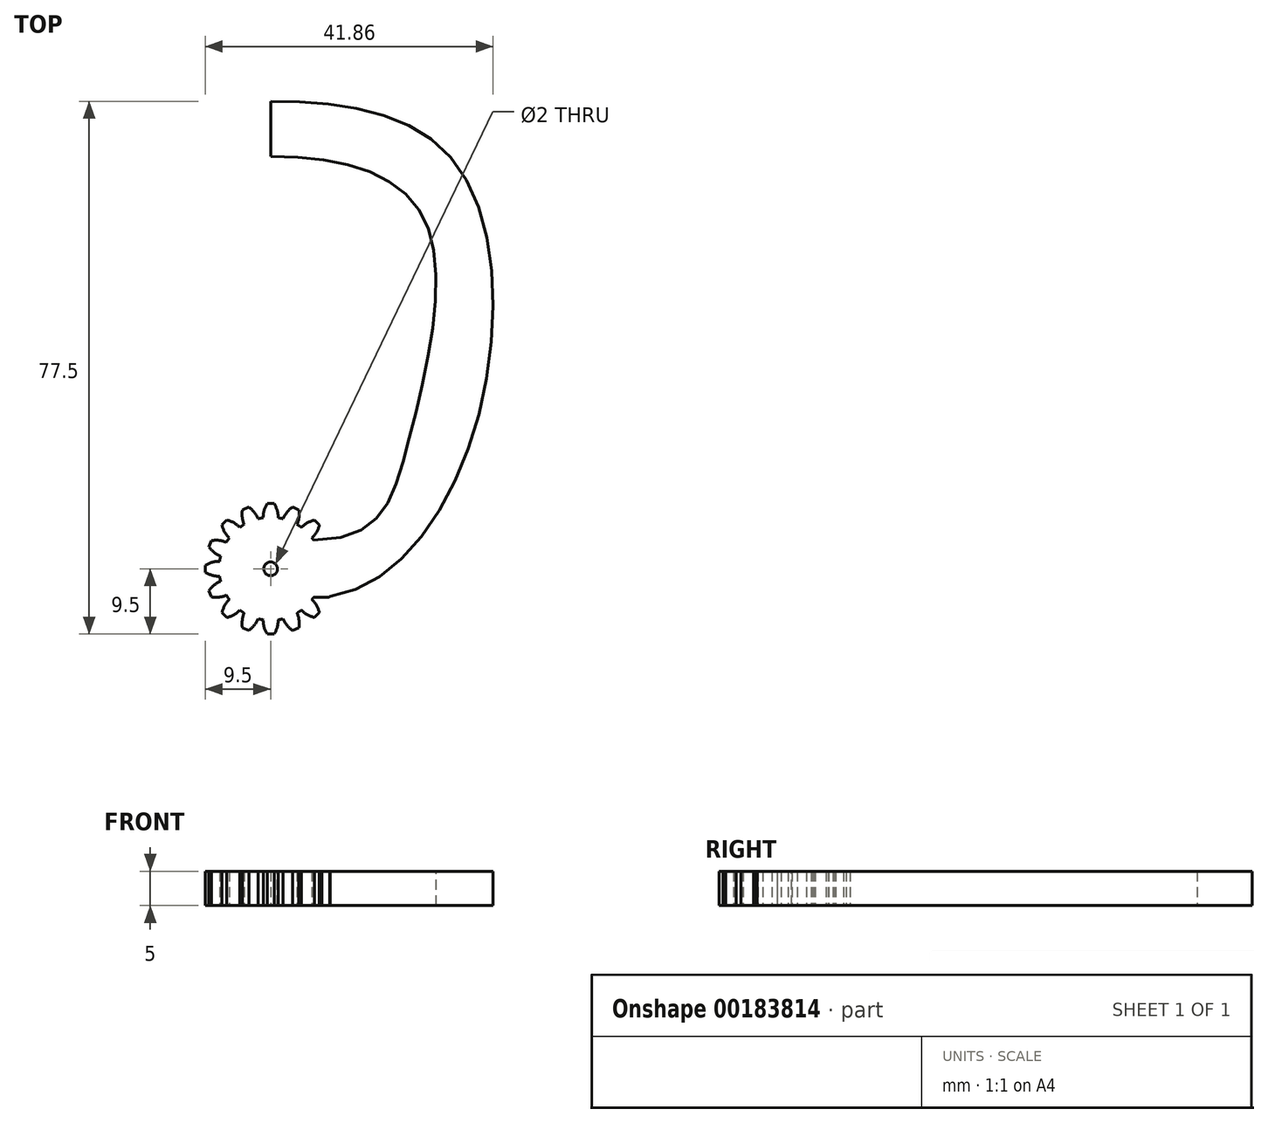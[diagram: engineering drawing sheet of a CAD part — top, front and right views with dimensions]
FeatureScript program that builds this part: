
annotation { "Feature Type Name" : "Feature", "Feature Type Description" : "" }
export const myFeature = defineFeature(function(context is Context, id is Id, definition is map)
    precondition{}
    {
        {
            var Q0;
            Q0=qCreatedBy(makeId("Top.planeOp"),FACE);
            var sketch = newSketch(context, id + "F0", { "sketchPlane" : qUnion([Q0])});
            skCircle(sketch, "E0", {"center": v(0, 0) * mm, "radius": 7.5 * mm});
            skLineSegment(sketch, "E1", {"start": v(0, 0) * mm, "end": v(0, 7.5) * mm, "construction": true});
            skLineSegment(sketch, "E2", {"start": v(0, 9.5) * mm, "end": v(-0.5, 9.5) * mm});
            skArc(sketch, "E3", {"start": v(-0.5, 9.5) * mm, "mid": v(-0.95, 8.5) * mm, "end": v(-1.09, 7.42) * mm});
            skArc(sketch, "E4.MirrorCS", {"start": v(0.5, 9.5) * mm, "mid": v(0.95, 8.5) * mm, "end": v(1.09, 7.42) * mm});
            skLineSegment(sketch, "E5.MirrorCS", {"start": v(0, 9.5) * mm, "end": v(0.5, 9.5) * mm});
            skArc(sketch, "E6.1.0", {"start": v(-4.1, 8.59) * mm, "mid": v(-4.13, 7.5) * mm, "end": v(-3.85, 6.44) * mm});
            skLineSegment(sketch, "E6.1.1", {"start": v(-3.64, 8.78) * mm, "end": v(-4.1, 8.59) * mm});
            skLineSegment(sketch, "E6.1.2", {"start": v(-3.64, 8.78) * mm, "end": v(-3.17, 8.97) * mm});
            skArc(sketch, "E6.1.3", {"start": v(-3.17, 8.97) * mm, "mid": v(-2.38, 8.22) * mm, "end": v(-1.83, 7.27) * mm});
            skArc(sketch, "E6.2.0", {"start": v(-7.07, 6.36) * mm, "mid": v(-6.69, 5.34) * mm, "end": v(-6.02, 4.48) * mm});
            skLineSegment(sketch, "E6.2.1", {"start": v(-6.72, 6.72) * mm, "end": v(-7.07, 6.36) * mm});
            skLineSegment(sketch, "E6.2.2", {"start": v(-6.72, 6.72) * mm, "end": v(-6.36, 7.07) * mm});
            skArc(sketch, "E6.2.3", {"start": v(-6.36, 7.07) * mm, "mid": v(-5.34, 6.69) * mm, "end": v(-4.48, 6.02) * mm});
            skArc(sketch, "E6.3.0", {"start": v(-8.97, 3.17) * mm, "mid": v(-8.22, 2.38) * mm, "end": v(-7.27, 1.83) * mm});
            skLineSegment(sketch, "E6.3.1", {"start": v(-8.78, 3.64) * mm, "end": v(-8.97, 3.17) * mm});
            skLineSegment(sketch, "E6.3.2", {"start": v(-8.78, 3.64) * mm, "end": v(-8.59, 4.1) * mm});
            skArc(sketch, "E6.3.3", {"start": v(-8.59, 4.1) * mm, "mid": v(-7.5, 4.13) * mm, "end": v(-6.44, 3.85) * mm});
            skArc(sketch, "E6.4.0", {"start": v(-9.5, -0.5) * mm, "mid": v(-8.5, -0.95) * mm, "end": v(-7.42, -1.09) * mm});
            skLineSegment(sketch, "E6.4.1", {"start": v(-9.5, 0) * mm, "end": v(-9.5, -0.5) * mm});
            skLineSegment(sketch, "E6.4.2", {"start": v(-9.5, 0) * mm, "end": v(-9.5, 0.5) * mm});
            skArc(sketch, "E6.4.3", {"start": v(-9.5, 0.5) * mm, "mid": v(-8.5, 0.95) * mm, "end": v(-7.42, 1.09) * mm});
            skArc(sketch, "E6.5.0", {"start": v(-8.59, -4.1) * mm, "mid": v(-7.5, -4.13) * mm, "end": v(-6.44, -3.85) * mm});
            skLineSegment(sketch, "E6.5.1", {"start": v(-8.78, -3.64) * mm, "end": v(-8.59, -4.1) * mm});
            skLineSegment(sketch, "E6.5.2", {"start": v(-8.78, -3.64) * mm, "end": v(-8.97, -3.17) * mm});
            skArc(sketch, "E6.5.3", {"start": v(-8.97, -3.17) * mm, "mid": v(-8.22, -2.38) * mm, "end": v(-7.27, -1.83) * mm});
            skArc(sketch, "E6.6.0", {"start": v(-6.36, -7.07) * mm, "mid": v(-5.34, -6.69) * mm, "end": v(-4.48, -6.02) * mm});
            skLineSegment(sketch, "E6.6.1", {"start": v(-6.72, -6.72) * mm, "end": v(-6.36, -7.07) * mm});
            skLineSegment(sketch, "E6.6.2", {"start": v(-6.72, -6.72) * mm, "end": v(-7.07, -6.36) * mm});
            skArc(sketch, "E6.6.3", {"start": v(-7.07, -6.36) * mm, "mid": v(-6.69, -5.34) * mm, "end": v(-6.02, -4.48) * mm});
            skArc(sketch, "E6.7.0", {"start": v(-3.17, -8.97) * mm, "mid": v(-2.38, -8.22) * mm, "end": v(-1.83, -7.27) * mm});
            skLineSegment(sketch, "E6.7.1", {"start": v(-3.64, -8.78) * mm, "end": v(-3.17, -8.97) * mm});
            skLineSegment(sketch, "E6.7.2", {"start": v(-3.64, -8.78) * mm, "end": v(-4.1, -8.59) * mm});
            skArc(sketch, "E6.7.3", {"start": v(-4.1, -8.59) * mm, "mid": v(-4.13, -7.5) * mm, "end": v(-3.85, -6.44) * mm});
            skArc(sketch, "E6.8.0", {"start": v(0.5, -9.5) * mm, "mid": v(0.95, -8.5) * mm, "end": v(1.09, -7.42) * mm});
            skLineSegment(sketch, "E6.8.1", {"start": v(0, -9.5) * mm, "end": v(0.5, -9.5) * mm});
            skLineSegment(sketch, "E6.8.2", {"start": v(0, -9.5) * mm, "end": v(-0.5, -9.5) * mm});
            skArc(sketch, "E6.8.3", {"start": v(-0.5, -9.5) * mm, "mid": v(-0.95, -8.5) * mm, "end": v(-1.09, -7.42) * mm});
            skArc(sketch, "E6.9.0", {"start": v(4.1, -8.59) * mm, "mid": v(4.13, -7.5) * mm, "end": v(3.85, -6.44) * mm});
            skLineSegment(sketch, "E6.9.1", {"start": v(3.64, -8.78) * mm, "end": v(4.1, -8.59) * mm});
            skLineSegment(sketch, "E6.9.2", {"start": v(3.64, -8.78) * mm, "end": v(3.17, -8.97) * mm});
            skArc(sketch, "E6.9.3", {"start": v(3.17, -8.97) * mm, "mid": v(2.38, -8.22) * mm, "end": v(1.83, -7.27) * mm});
            skArc(sketch, "E6.10.0", {"start": v(7.07, -6.36) * mm, "mid": v(6.69, -5.34) * mm, "end": v(6.02, -4.48) * mm});
            skLineSegment(sketch, "E6.10.1", {"start": v(6.72, -6.72) * mm, "end": v(7.07, -6.36) * mm});
            skLineSegment(sketch, "E6.10.2", {"start": v(6.72, -6.72) * mm, "end": v(6.36, -7.07) * mm});
            skArc(sketch, "E6.10.3", {"start": v(6.36, -7.07) * mm, "mid": v(5.34, -6.69) * mm, "end": v(4.48, -6.02) * mm});
            skArc(sketch, "E6.11.0", {"start": v(8.97, -3.17) * mm, "mid": v(8.22, -2.38) * mm, "end": v(7.27, -1.83) * mm});
            skLineSegment(sketch, "E6.11.1", {"start": v(8.78, -3.64) * mm, "end": v(8.97, -3.17) * mm});
            skLineSegment(sketch, "E6.11.2", {"start": v(8.78, -3.64) * mm, "end": v(8.59, -4.1) * mm});
            skArc(sketch, "E6.11.3", {"start": v(8.59, -4.1) * mm, "mid": v(7.5, -4.13) * mm, "end": v(6.44, -3.85) * mm});
            skArc(sketch, "E6.12.0", {"start": v(9.5, 0.5) * mm, "mid": v(8.5, 0.95) * mm, "end": v(7.42, 1.09) * mm});
            skLineSegment(sketch, "E6.12.1", {"start": v(9.5, 0) * mm, "end": v(9.5, 0.5) * mm});
            skLineSegment(sketch, "E6.12.2", {"start": v(9.5, 0) * mm, "end": v(9.5, -0.5) * mm});
            skArc(sketch, "E6.12.3", {"start": v(9.5, -0.5) * mm, "mid": v(8.5, -0.95) * mm, "end": v(7.42, -1.09) * mm});
            skArc(sketch, "E6.13.0", {"start": v(8.59, 4.1) * mm, "mid": v(7.5, 4.13) * mm, "end": v(6.44, 3.85) * mm});
            skLineSegment(sketch, "E6.13.1", {"start": v(8.78, 3.64) * mm, "end": v(8.59, 4.1) * mm});
            skLineSegment(sketch, "E6.13.2", {"start": v(8.78, 3.64) * mm, "end": v(8.97, 3.17) * mm});
            skArc(sketch, "E6.13.3", {"start": v(8.97, 3.17) * mm, "mid": v(8.22, 2.38) * mm, "end": v(7.27, 1.83) * mm});
            skArc(sketch, "E6.14.0", {"start": v(6.36, 7.07) * mm, "mid": v(5.34, 6.69) * mm, "end": v(4.48, 6.02) * mm});
            skLineSegment(sketch, "E6.14.1", {"start": v(6.72, 6.72) * mm, "end": v(6.36, 7.07) * mm});
            skLineSegment(sketch, "E6.14.2", {"start": v(6.72, 6.72) * mm, "end": v(7.07, 6.36) * mm});
            skArc(sketch, "E6.14.3", {"start": v(7.07, 6.36) * mm, "mid": v(6.69, 5.34) * mm, "end": v(6.02, 4.48) * mm});
            skArc(sketch, "E6.15.0", {"start": v(3.17, 8.97) * mm, "mid": v(2.38, 8.22) * mm, "end": v(1.83, 7.27) * mm});
            skLineSegment(sketch, "E6.15.1", {"start": v(3.64, 8.78) * mm, "end": v(3.17, 8.97) * mm});
            skLineSegment(sketch, "E6.15.2", {"start": v(3.64, 8.78) * mm, "end": v(4.1, 8.59) * mm});
            skArc(sketch, "E6.15.3", {"start": v(4.1, 8.59) * mm, "mid": v(4.13, 7.5) * mm, "end": v(3.85, 6.44) * mm});
            skSolve(sketch);
        }
        {
            var Q0;
            Q0=qSketchRegion(id+"F0",true);
            extrude(context, id + "F1", {"entities" : qUnion([Q0]), "depth" : 5 * mm});
        }
        {
            var Q0;
            Q0=makeQuery(id+"F1.opExtrude","CAP_FACE",FACE,{"disambiguationData":[OSD([sQuery(id+"F0.wireOp",EDGE,"E0"),sQuery(id+"F0.wireOp",EDGE,"E2"),sQuery(id+"F0.wireOp",EDGE,"E3"),sQuery(id+"F0.wireOp",EDGE,"E4.MirrorCS"),sQuery(id+"F0.wireOp",EDGE,"E5.MirrorCS"),sQuery(id+"F0.wireOp",EDGE,"E6.1.0"),sQuery(id+"F0.wireOp",EDGE,"E6.1.1"),sQuery(id+"F0.wireOp",EDGE,"E6.1.2"),sQuery(id+"F0.wireOp",EDGE,"E6.1.3"),sQuery(id+"F0.wireOp",EDGE,"E6.2.0"),sQuery(id+"F0.wireOp",EDGE,"E6.2.1"),sQuery(id+"F0.wireOp",EDGE,"E6.2.2"),sQuery(id+"F0.wireOp",EDGE,"E6.2.3"),sQuery(id+"F0.wireOp",EDGE,"E6.3.0"),sQuery(id+"F0.wireOp",EDGE,"E6.3.1"),sQuery(id+"F0.wireOp",EDGE,"E6.3.2"),sQuery(id+"F0.wireOp",EDGE,"E6.3.3"),sQuery(id+"F0.wireOp",EDGE,"E6.4.0"),sQuery(id+"F0.wireOp",EDGE,"E6.4.1"),sQuery(id+"F0.wireOp",EDGE,"E6.4.2"),sQuery(id+"F0.wireOp",EDGE,"E6.4.3"),sQuery(id+"F0.wireOp",EDGE,"E6.5.0"),sQuery(id+"F0.wireOp",EDGE,"E6.5.1"),sQuery(id+"F0.wireOp",EDGE,"E6.5.2"),sQuery(id+"F0.wireOp",EDGE,"E6.5.3"),sQuery(id+"F0.wireOp",EDGE,"E6.6.0"),sQuery(id+"F0.wireOp",EDGE,"E6.6.1"),sQuery(id+"F0.wireOp",EDGE,"E6.6.2"),sQuery(id+"F0.wireOp",EDGE,"E6.6.3"),sQuery(id+"F0.wireOp",EDGE,"E6.7.0"),sQuery(id+"F0.wireOp",EDGE,"E6.7.1"),sQuery(id+"F0.wireOp",EDGE,"E6.7.2"),sQuery(id+"F0.wireOp",EDGE,"E6.7.3"),sQuery(id+"F0.wireOp",EDGE,"E6.8.0"),sQuery(id+"F0.wireOp",EDGE,"E6.8.1"),sQuery(id+"F0.wireOp",EDGE,"E6.8.2"),sQuery(id+"F0.wireOp",EDGE,"E6.8.3"),sQuery(id+"F0.wireOp",EDGE,"E6.9.0"),sQuery(id+"F0.wireOp",EDGE,"E6.9.1"),sQuery(id+"F0.wireOp",EDGE,"E6.9.2"),sQuery(id+"F0.wireOp",EDGE,"E6.9.3"),sQuery(id+"F0.wireOp",EDGE,"E6.10.0"),sQuery(id+"F0.wireOp",EDGE,"E6.10.1"),sQuery(id+"F0.wireOp",EDGE,"E6.10.2"),sQuery(id+"F0.wireOp",EDGE,"E6.10.3"),sQuery(id+"F0.wireOp",EDGE,"E6.11.0"),sQuery(id+"F0.wireOp",EDGE,"E6.11.1"),sQuery(id+"F0.wireOp",EDGE,"E6.11.2"),sQuery(id+"F0.wireOp",EDGE,"E6.11.3"),sQuery(id+"F0.wireOp",EDGE,"E6.12.0"),sQuery(id+"F0.wireOp",EDGE,"E6.12.1"),sQuery(id+"F0.wireOp",EDGE,"E6.12.2"),sQuery(id+"F0.wireOp",EDGE,"E6.12.3"),sQuery(id+"F0.wireOp",EDGE,"E6.13.0"),sQuery(id+"F0.wireOp",EDGE,"E6.13.1"),sQuery(id+"F0.wireOp",EDGE,"E6.13.2"),sQuery(id+"F0.wireOp",EDGE,"E6.13.3"),sQuery(id+"F0.wireOp",EDGE,"E6.14.0"),sQuery(id+"F0.wireOp",EDGE,"E6.14.1"),sQuery(id+"F0.wireOp",EDGE,"E6.14.2"),sQuery(id+"F0.wireOp",EDGE,"E6.14.3"),sQuery(id+"F0.wireOp",EDGE,"E6.15.0"),sQuery(id+"F0.wireOp",EDGE,"E6.15.1"),sQuery(id+"F0.wireOp",EDGE,"E6.15.2"),sQuery(id+"F0.wireOp",EDGE,"E6.15.3")])],"isStart":false});
            var sketch = newSketch(context, id + "F2", { "sketchPlane" : qUnion([Q0])});
            skCircle(sketch, "E7", {"center": v(0, 0) * mm, "radius": 1 * mm});
            skSolve(sketch);
        }
        {
            var Q0;
            Q0=qSketchRegion(id+"F2",true);
            extrude(context, id + "F3", {"entities" : qUnion([Q0]), "operationType" : NewBodyOperationType.REMOVE, "endBound" : BoundingType.THROUGH_ALL, "oppositeDirection" : true, "depth" : 25 * mm});
        }
        {
            var Q0;
            Q0=qCreatedBy(makeId("Top.planeOp"),FACE);
            var sketch = newSketch(context, id + "F4", { "sketchPlane" : qUnion([Q0])});
            skLineSegment(sketch, "E8", {"start": v(0, 60) * mm, "end": v(0, 68) * mm});
            skFitSpline(sketch, "E9", {"points": [v(0, 60) * mm, v(22.3, 50.96) * mm, v(19.95, 18.14) * mm, v(6.24, 4.17) * mm], "startDerivative": vector(92.13, 0) * mm, "endDerivative": vector(-102.17, 0) * mm});
            skFitSpline(sketch, "E10", {"points": [v(0, 68) * mm, v(26.74, 59.2) * mm, v(28.7, 17.34) * mm, v(6.24, -4.17) * mm], "startDerivative": vector(98.15, 0) * mm, "endDerivative": vector(-93.36, 0) * mm});
            skLineSegment(sketch, "E11", {"start": v(6.24, 4.17) * mm, "end": v(6.24, -4.17) * mm});
            skSolve(sketch);
        }
        {
            var Q0;
            Q0 = qSketchRegion(id + "F4", true);
            var Q1;
            Q1=makeQuery(id+"F1.opExtrude","CAP_FACE",FACE,{"disambiguationData":[OSD([sQuery(id+"F0.wireOp",EDGE,"E0"),sQuery(id+"F0.wireOp",EDGE,"E2"),sQuery(id+"F0.wireOp",EDGE,"E3"),sQuery(id+"F0.wireOp",EDGE,"E4.MirrorCS"),sQuery(id+"F0.wireOp",EDGE,"E5.MirrorCS"),sQuery(id+"F0.wireOp",EDGE,"E6.1.0"),sQuery(id+"F0.wireOp",EDGE,"E6.1.1"),sQuery(id+"F0.wireOp",EDGE,"E6.1.2"),sQuery(id+"F0.wireOp",EDGE,"E6.1.3"),sQuery(id+"F0.wireOp",EDGE,"E6.2.0"),sQuery(id+"F0.wireOp",EDGE,"E6.2.1"),sQuery(id+"F0.wireOp",EDGE,"E6.2.2"),sQuery(id+"F0.wireOp",EDGE,"E6.2.3"),sQuery(id+"F0.wireOp",EDGE,"E6.3.0"),sQuery(id+"F0.wireOp",EDGE,"E6.3.1"),sQuery(id+"F0.wireOp",EDGE,"E6.3.2"),sQuery(id+"F0.wireOp",EDGE,"E6.3.3"),sQuery(id+"F0.wireOp",EDGE,"E6.4.0"),sQuery(id+"F0.wireOp",EDGE,"E6.4.1"),sQuery(id+"F0.wireOp",EDGE,"E6.4.2"),sQuery(id+"F0.wireOp",EDGE,"E6.4.3"),sQuery(id+"F0.wireOp",EDGE,"E6.5.0"),sQuery(id+"F0.wireOp",EDGE,"E6.5.1"),sQuery(id+"F0.wireOp",EDGE,"E6.5.2"),sQuery(id+"F0.wireOp",EDGE,"E6.5.3"),sQuery(id+"F0.wireOp",EDGE,"E6.6.0"),sQuery(id+"F0.wireOp",EDGE,"E6.6.1"),sQuery(id+"F0.wireOp",EDGE,"E6.6.2"),sQuery(id+"F0.wireOp",EDGE,"E6.6.3"),sQuery(id+"F0.wireOp",EDGE,"E6.7.0"),sQuery(id+"F0.wireOp",EDGE,"E6.7.1"),sQuery(id+"F0.wireOp",EDGE,"E6.7.2"),sQuery(id+"F0.wireOp",EDGE,"E6.7.3"),sQuery(id+"F0.wireOp",EDGE,"E6.8.0"),sQuery(id+"F0.wireOp",EDGE,"E6.8.1"),sQuery(id+"F0.wireOp",EDGE,"E6.8.2"),sQuery(id+"F0.wireOp",EDGE,"E6.8.3"),sQuery(id+"F0.wireOp",EDGE,"E6.9.0"),sQuery(id+"F0.wireOp",EDGE,"E6.9.1"),sQuery(id+"F0.wireOp",EDGE,"E6.9.2"),sQuery(id+"F0.wireOp",EDGE,"E6.9.3"),sQuery(id+"F0.wireOp",EDGE,"E6.10.0"),sQuery(id+"F0.wireOp",EDGE,"E6.10.1"),sQuery(id+"F0.wireOp",EDGE,"E6.10.2"),sQuery(id+"F0.wireOp",EDGE,"E6.10.3"),sQuery(id+"F0.wireOp",EDGE,"E6.11.0"),sQuery(id+"F0.wireOp",EDGE,"E6.11.1"),sQuery(id+"F0.wireOp",EDGE,"E6.11.2"),sQuery(id+"F0.wireOp",EDGE,"E6.11.3"),sQuery(id+"F0.wireOp",EDGE,"E6.12.0"),sQuery(id+"F0.wireOp",EDGE,"E6.12.1"),sQuery(id+"F0.wireOp",EDGE,"E6.12.2"),sQuery(id+"F0.wireOp",EDGE,"E6.12.3"),sQuery(id+"F0.wireOp",EDGE,"E6.13.0"),sQuery(id+"F0.wireOp",EDGE,"E6.13.1"),sQuery(id+"F0.wireOp",EDGE,"E6.13.2"),sQuery(id+"F0.wireOp",EDGE,"E6.13.3"),sQuery(id+"F0.wireOp",EDGE,"E6.14.0"),sQuery(id+"F0.wireOp",EDGE,"E6.14.1"),sQuery(id+"F0.wireOp",EDGE,"E6.14.2"),sQuery(id+"F0.wireOp",EDGE,"E6.14.3"),sQuery(id+"F0.wireOp",EDGE,"E6.15.0"),sQuery(id+"F0.wireOp",EDGE,"E6.15.1"),sQuery(id+"F0.wireOp",EDGE,"E6.15.2"),sQuery(id+"F0.wireOp",EDGE,"E6.15.3")])],"isStart":false});
            extrude(context, id + "F5", {"entities" : qUnion([Q0]), "operationType" : NewBodyOperationType.ADD, "endBound" : BoundingType.UP_TO_SURFACE, "endBoundEntityFace" : qUnion([Q1]), "depth" : 25 * mm});
        }
    });
